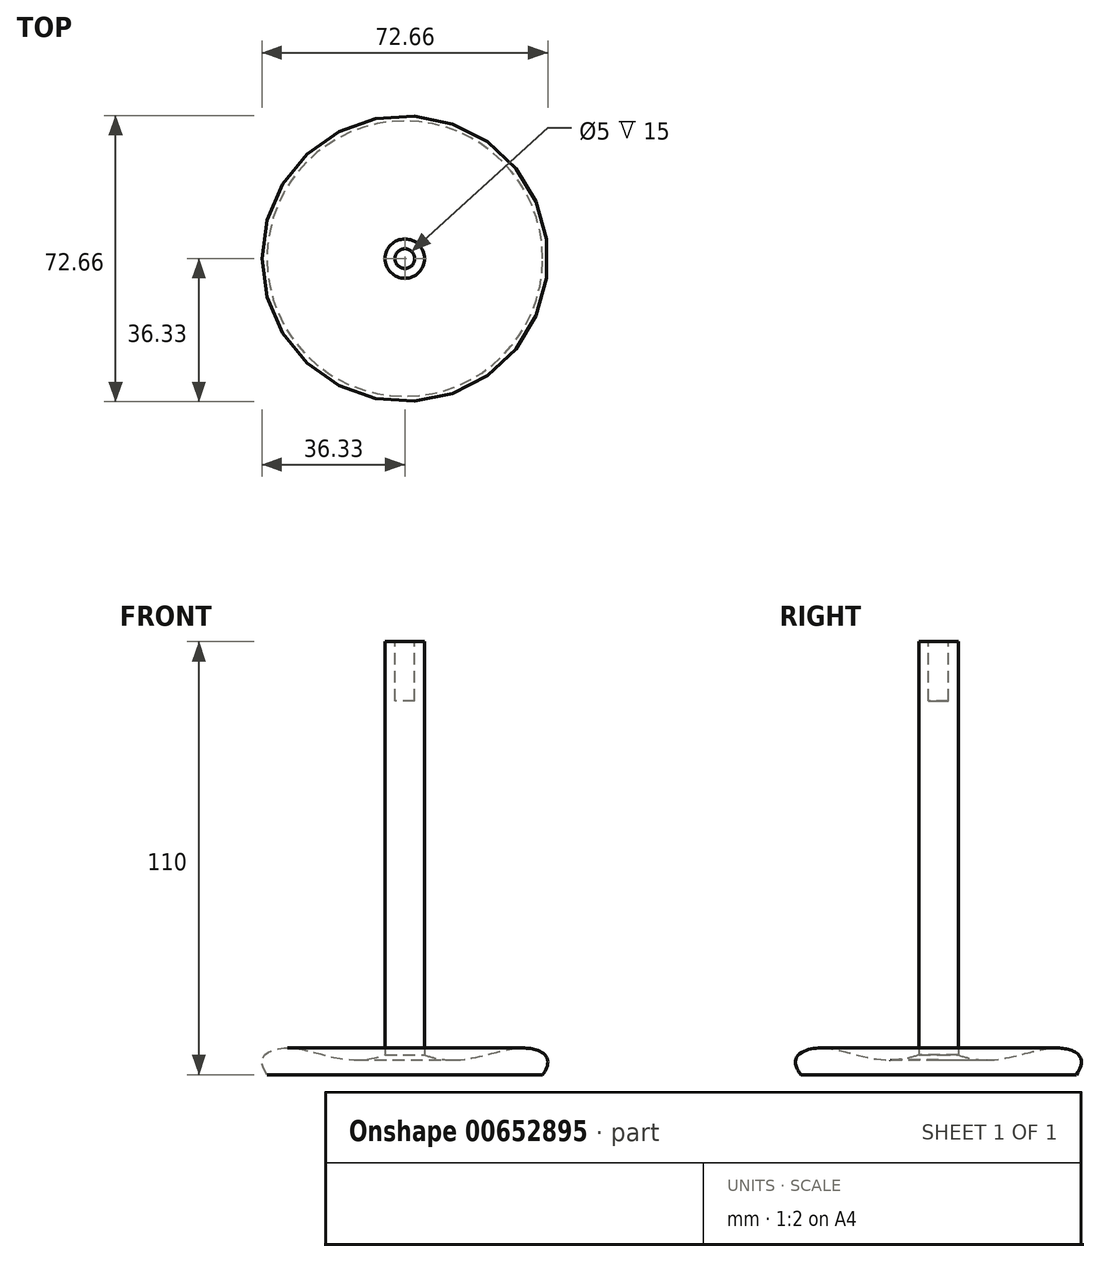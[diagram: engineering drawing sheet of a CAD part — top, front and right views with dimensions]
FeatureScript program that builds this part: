
annotation { "Feature Type Name" : "Feature", "Feature Type Description" : "" }
export const myFeature = defineFeature(function(context is Context, id is Id, definition is map)
    precondition{}
    {
        {
            var Q0;
            Q0=qCreatedBy(makeId("Right.planeOp"),FACE);
            var sketch = newSketch(context, id + "F0", { "sketchPlane" : qUnion([Q0])});
            skLineSegment(sketch, "E0", {"start": v(0, 0) * mm, "end": v(-35, 0) * mm});
            skLineSegment(sketch, "E1", {"start": v(0, 0) * mm, "end": v(0, 110) * mm});
            skLineSegment(sketch, "E2", {"start": v(0, 110) * mm, "end": v(-5, 110) * mm});
            skLineSegment(sketch, "E3", {"start": v(-5, 110) * mm, "end": v(-5, 5) * mm});
            skFitSpline(sketch, "E4", {"points": [v(-35, 0) * mm, v(-30.05, 6.78) * mm, v(-5, 5) * mm], "startDerivative": vector(-29.17, 39.06) * mm, "endDerivative": vector(49.08, 17.62) * mm});
            skSolve(sketch);
        }
        {
            var Q0;
            Q0=makeQuery(id+"F0.imprint","IMPRINT",FACE,{"disambiguationData":[TD([[makeQuery(id+"F0.imprint","IMPRINT",EDGE,{"derivedFrom":sQuery(id+"F0.wireOp",EDGE,"E0")}),-1.0]])]});
            var Q1;
            Q1=sQuery(id+"F0.wireOp",EDGE,"E1");
            revolve(context, id + "F1", {"entities" : qUnion([Q0]), "axis" : qUnion([Q1]), "revolveType" : RevolveType.FULL});
        }
        {
            var Q0;
            Q0=makeQuery(id+"F1.opRevolve","SWEPT_FACE",FACE,{"disambiguationData":[OSD([sQuery(id+"F0.wireOp",EDGE,"E2")])]});
            var sketch = newSketch(context, id + "F2", { "sketchPlane" : qUnion([Q0])});
            skCircle(sketch, "E5", {"center": v(0, 0) * mm, "radius": 2.5 * mm});
            skSolve(sketch);
        }
        {
            var Q0;
            Q0 = qSketchRegion(id + "F2", true);
            extrude(context, id + "F3", {"entities" : qUnion([Q0]), "operationType" : NewBodyOperationType.REMOVE, "oppositeDirection" : true, "depth" : 15 * mm, "offsetDistance" : 25 * mm});
        }
    });
